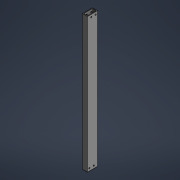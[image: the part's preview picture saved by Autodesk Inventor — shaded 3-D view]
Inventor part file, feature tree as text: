
AUTODESK INVENTOR PART (.ipt)
format: ipt  version: 2022.2 (Build 262287000, 287)  size: 101,888 bytes
history: native  units: mm (DEFAULTED — no unit token found)
features: sketch x2, extrude x1, hole x1
ambient origin geometry x8: Origin, YZ Plane, XZ Plane, XY Plane, X Axis, Y Axis, Z Axis, Center Point
bodies: Solid1 (feature_tree)
feature tree (4):
  extrude  "Extrusion1"  Depth=25.4mm
  hole  "Hole1"  [1 undecoded]
  sketch  "Sketch1"  dims[d0=50.8mm d1=25.4mm]
  sketch  "Sketch2"  dims[d2=3.175mm d3=3.175mm d4=3.175mm d5=3.175mm d6=685.8mm d7=0.0mm d8=9.525mm d9=19.05mm d10=12.7mm d11=12.7mm d12=12.7mm d13=19.05mm d14=12.7mm d15=9.525mm d16=6.5278mm d17=19.05mm d18=9.525mm d19=6.35mm d20=14.3117mm d21=50.8mm d22=20.594885mm d23=19.05mm d24=20.594885mm d25=1.5875mm d26=19.05mm d27=9.525mm d28=9.525mm d29=14.3117mm d30=19.05mm d31=20.594885mm d32=1.5875mm d33=19.05mm d34=9.525mm]
note: 1 required parameter value undecoded (feature->parameter linkage not recoverable at this tier; creation-order binding heuristic only, values carry confidence <= 0.55)
